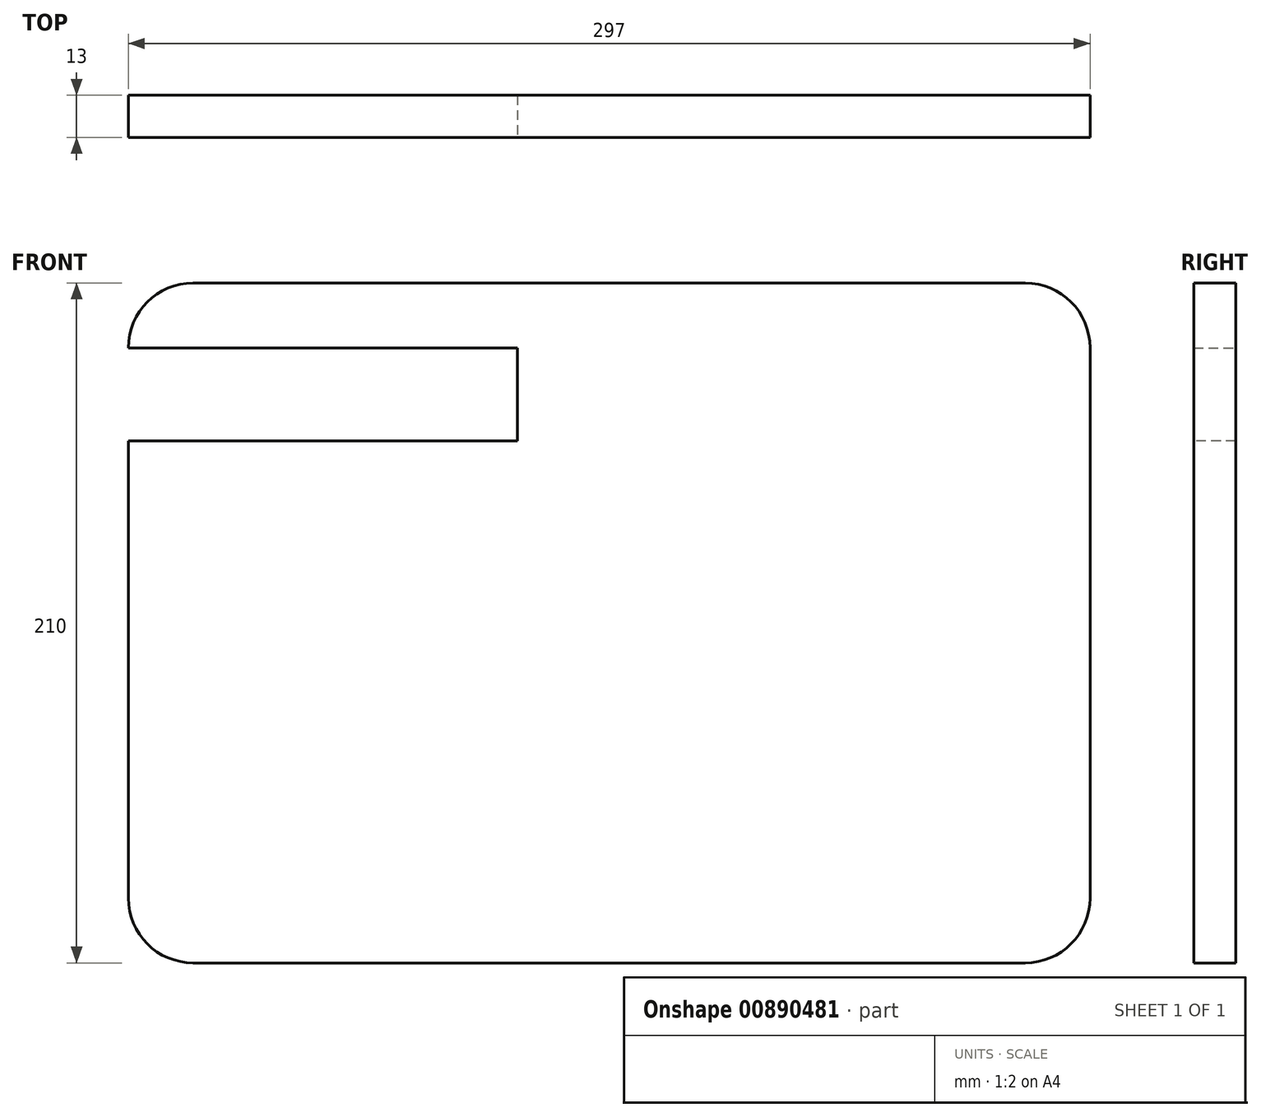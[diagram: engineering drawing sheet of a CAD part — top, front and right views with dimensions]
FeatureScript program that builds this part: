
annotation { "Feature Type Name" : "Feature", "Feature Type Description" : "" }
export const myFeature = defineFeature(function(context is Context, id is Id, definition is map)
    precondition{}
    {
        {
            var Q0;
            Q0=qCreatedBy(makeId("Front.planeOp"),FACE);
            var sketch = newSketch(context, id + "F0", { "sketchPlane" : qUnion([Q0])});
            skLineSegment(sketch, "E0.bottom", {"start": v(-74.37, 123.41) * mm, "end": v(182.63, 123.41) * mm});
            skLineSegment(sketch, "E0.top", {"start": v(-74.37, -86.59) * mm, "end": v(182.63, -86.59) * mm});
            skLineSegment(sketch, "E0.left", {"start": v(-94.37, 103.41) * mm, "end": v(-94.37, -66.59) * mm});
            skLineSegment(sketch, "E0.right", {"start": v(202.63, 103.41) * mm, "end": v(202.63, -66.59) * mm});
            skPoint(sketch, "E1.visualSharp", {"position": v(-94.37, 123.41) * mm});
            skArc(sketch, "E1.filletArc", {"start": v(-74.37, 123.41) * mm, "mid": v(-88.51, 117.55) * mm, "end": v(-94.37, 103.41) * mm});
            skPoint(sketch, "E2.visualSharp", {"position": v(202.63, 123.41) * mm});
            skArc(sketch, "E2.filletArc", {"start": v(202.63, 103.41) * mm, "mid": v(196.77, 117.55) * mm, "end": v(182.63, 123.41) * mm});
            skPoint(sketch, "E3.visualSharp", {"position": v(202.63, -86.59) * mm});
            skArc(sketch, "E3.filletArc", {"start": v(182.63, -86.59) * mm, "mid": v(196.77, -80.73) * mm, "end": v(202.63, -66.59) * mm});
            skPoint(sketch, "E4.visualSharp", {"position": v(-94.37, -86.59) * mm});
            skArc(sketch, "E4.filletArc", {"start": v(-94.37, -66.59) * mm, "mid": v(-88.51, -80.73) * mm, "end": v(-74.37, -86.59) * mm});
            skSolve(sketch);
        }
        {
            var Q0;
            Q0 = qSketchRegion(id + "F0", true);
            extrude(context, id + "F1", {"entities" : qUnion([Q0]), "depth" : 13 * mm, "offsetDistance" : 25 * mm});
        }
        {
            var Q0;
            Q0=makeQuery(id+"F1.opExtrude","CAP_FACE",FACE,{"disambiguationData":[OSD([sQuery(id+"F0.wireOp",EDGE,"E0.bottom"),sQuery(id+"F0.wireOp",EDGE,"E0.top"),sQuery(id+"F0.wireOp",EDGE,"E0.left"),sQuery(id+"F0.wireOp",EDGE,"E0.right"),sQuery(id+"F0.wireOp",EDGE,"E1.filletArc"),sQuery(id+"F0.wireOp",EDGE,"E2.filletArc"),sQuery(id+"F0.wireOp",EDGE,"E3.filletArc"),sQuery(id+"F0.wireOp",EDGE,"E4.filletArc")])],"isStart":false});
            var sketch = newSketch(context, id + "F2", { "sketchPlane" : qUnion([Q0])});
            skLineSegment(sketch, "E5.bottom", {"start": v(-94.37, 103.41) * mm, "end": v(25.74, 103.41) * mm});
            skLineSegment(sketch, "E5.top", {"start": v(-94.37, 74.7) * mm, "end": v(25.74, 74.7) * mm});
            skLineSegment(sketch, "E5.left", {"start": v(-94.37, 103.41) * mm, "end": v(-94.37, 74.7) * mm});
            skLineSegment(sketch, "E5.right", {"start": v(25.74, 103.41) * mm, "end": v(25.74, 74.7) * mm});
            skSolve(sketch);
        }
        {
            var Q0;
            Q0=makeQuery(id+"F2.imprint","IMPRINT",FACE,{"disambiguationData":[TD([[makeQuery(id+"F2.imprint","IMPRINT",EDGE,{"derivedFrom":sQuery(id+"F2.wireOp",EDGE,"E5.bottom")}),1.0]])]});
            var sketch = newSketch(context, id + "F3", { "sketchPlane" : qUnion([Q0])});
            skSolve(sketch);
        }
        {
            var Q0;
            Q0=makeQuery(id+"F3.imprint","IMPRINT",FACE,{"disambiguationData":[TD([[makeQuery(id+"F3.imprint","IMPRINT",EDGE,{"derivedFrom":makeQuery(id+"F2.imprint","IMPRINT",EDGE,{"derivedFrom":sQuery(id+"F2.wireOp",EDGE,"E5.bottom")})}),1.0]])]});
            var sketch = newSketch(context, id + "F4", { "sketchPlane" : qUnion([Q0])});
            skSolve(sketch);
        }
        {
            var Q0;
            Q0=makeQuery(id+"F2.imprint","IMPRINT",FACE,{"disambiguationData":[TD([[makeQuery(id+"F2.imprint","IMPRINT",EDGE,{"derivedFrom":sQuery(id+"F2.wireOp",EDGE,"E5.bottom")}),-1.0]])]});
            extrude(context, id + "F5", {"entities" : qUnion([Q0]), "operationType" : NewBodyOperationType.REMOVE, "oppositeDirection" : true, "depth" : 25 * mm, "offsetDistance" : 25 * mm});
        }
    });
